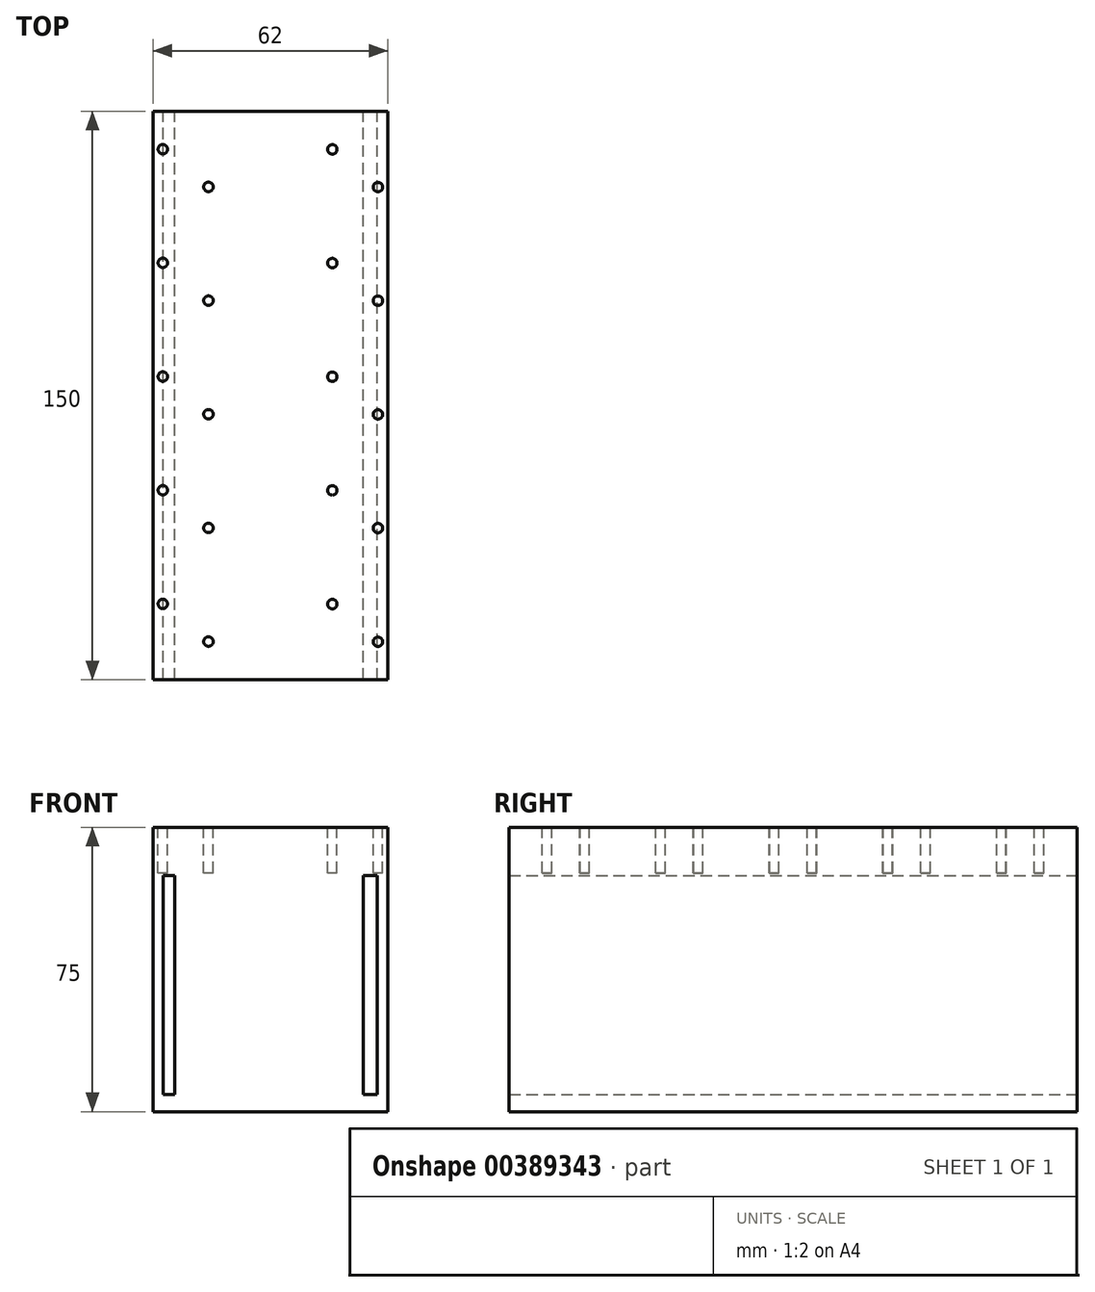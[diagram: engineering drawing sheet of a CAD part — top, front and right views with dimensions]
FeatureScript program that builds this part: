
annotation { "Feature Type Name" : "Feature", "Feature Type Description" : "" }
export const myFeature = defineFeature(function(context is Context, id is Id, definition is map)
    precondition{}
    {
        {
            var Q0;
            Q0=qCreatedBy(makeId("Top.planeOp"),FACE);
            var sketch = newSketch(context, id + "F0", { "sketchPlane" : qUnion([Q0])});
            skLineSegment(sketch, "E0.bottom", {"start": v(31, 75) * mm, "end": v(-31, 75) * mm});
            skLineSegment(sketch, "E0.top", {"start": v(31, -75) * mm, "end": v(-31, -75) * mm});
            skLineSegment(sketch, "E0.left", {"start": v(31, 75) * mm, "end": v(31, -75) * mm});
            skLineSegment(sketch, "E0.right", {"start": v(-31, 75) * mm, "end": v(-31, -75) * mm});
            skPoint(sketch, "E0.middle", {"position": v(0, 0) * mm});
            skCircle(sketch, "E1", {"center": v(-28.4, -55) * mm, "radius": 1.25 * mm});
            skCircle(sketch, "E2", {"center": v(-16.35, -64.95) * mm, "radius": 1.25 * mm});
            skCircle(sketch, "E3", {"center": v(-28.4, -25) * mm, "radius": 1.25 * mm});
            skCircle(sketch, "E4", {"center": v(-16.35, -34.95) * mm, "radius": 1.25 * mm});
            skCircle(sketch, "E5", {"center": v(-28.4, 5) * mm, "radius": 1.25 * mm});
            skCircle(sketch, "E6", {"center": v(-16.35, -4.95) * mm, "radius": 1.25 * mm});
            skCircle(sketch, "E7", {"center": v(-28.4, 35) * mm, "radius": 1.25 * mm});
            skCircle(sketch, "E8", {"center": v(-16.35, 25.05) * mm, "radius": 1.25 * mm});
            skCircle(sketch, "E9", {"center": v(-28.4, 65) * mm, "radius": 1.25 * mm});
            skCircle(sketch, "E10", {"center": v(-16.35, 55.05) * mm, "radius": 1.25 * mm});
            skCircle(sketch, "E11", {"center": v(28.4, 55) * mm, "radius": 1.25 * mm});
            skCircle(sketch, "E12", {"center": v(16.35, 64.95) * mm, "radius": 1.25 * mm});
            skCircle(sketch, "E13", {"center": v(28.4, 25) * mm, "radius": 1.25 * mm});
            skCircle(sketch, "E14", {"center": v(16.35, 34.95) * mm, "radius": 1.25 * mm});
            skCircle(sketch, "E15", {"center": v(28.4, -5) * mm, "radius": 1.25 * mm});
            skCircle(sketch, "E16", {"center": v(16.35, 4.95) * mm, "radius": 1.25 * mm});
            skCircle(sketch, "E17", {"center": v(28.4, -35) * mm, "radius": 1.25 * mm});
            skCircle(sketch, "E18", {"center": v(16.35, -25.05) * mm, "radius": 1.25 * mm});
            skCircle(sketch, "E19", {"center": v(28.4, -65) * mm, "radius": 1.25 * mm});
            skCircle(sketch, "E20", {"center": v(16.35, -55.05) * mm, "radius": 1.25 * mm});
            skSolve(sketch);
        }
        {
            var Q0;
            {var subQ0=sQuery(id+"F0.wireOp",EDGE,"E0.left");var subQ1=sQuery(id+"F0.wireOp",EDGE,"E0.bottom");var subQ2=makeQuery(id+"F0.imprint","INTERSECT",VERTEX,{"derivedFrom":[subQ1,subQ0]});Q0=makeQuery(id+"F0.imprint","IMPRINT",FACE,{"disambiguationData":[TD([[makeQuery(id+"F0.imprint","IMPRINT",EDGE,{"disambiguationData":[TD([[subQ2,-1.0]])],"derivedFrom":subQ0}),-1.0]])]});}
            var Q1;
            Q1=makeQuery(id+"F0.imprint","IMPRINT",FACE,{"disambiguationData":[TD([[makeQuery(id+"F0.imprint","IMPRINT",EDGE,{"derivedFrom":sQuery(id+"F0.wireOp",EDGE,"E11")}),-1.0]])]});
            var Q2;
            {var subQ0=sQuery(id+"F0.wireOp",EDGE,"0Nzpq0zW-OAD0-kYl2-P6jv-PgwHEek2wbxL");var subQ1=sQuery(id+"F0.wireOp",EDGE,"E0.left");var subQ2=makeQuery(id+"F0.imprint","INTERSECT",VERTEX,{"derivedFrom":[subQ1,subQ0]});Q2=makeQuery(id+"F0.imprint","IMPRINT",FACE,{"disambiguationData":[TD([[makeQuery(id+"F0.imprint","IMPRINT",EDGE,{"disambiguationData":[TD([[subQ2,-1.0]])],"derivedFrom":subQ1}),-1.0]])]});}
            var Q3;
            Q3=makeQuery(id+"F0.imprint","IMPRINT",FACE,{"disambiguationData":[TD([[makeQuery(id+"F0.imprint","IMPRINT",EDGE,{"derivedFrom":sQuery(id+"F0.wireOp",EDGE,"E13")}),-1.0]])]});
            var Q4;
            {var subQ0=sQuery(id+"F0.wireOp",EDGE,"HYNGpQ2a-oc8r-ey4b-d9cL-286HAeqs42Th");var subQ1=sQuery(id+"F0.wireOp",EDGE,"E0.left");var subQ2=makeQuery(id+"F0.imprint","INTERSECT",VERTEX,{"derivedFrom":[subQ1,subQ0]});Q4=makeQuery(id+"F0.imprint","IMPRINT",FACE,{"disambiguationData":[TD([[makeQuery(id+"F0.imprint","IMPRINT",EDGE,{"disambiguationData":[TD([[subQ2,-1.0]])],"derivedFrom":subQ1}),-1.0]])]});}
            var Q5;
            Q5=makeQuery(id+"F0.imprint","IMPRINT",FACE,{"disambiguationData":[TD([[makeQuery(id+"F0.imprint","IMPRINT",EDGE,{"derivedFrom":sQuery(id+"F0.wireOp",EDGE,"E15")}),-1.0]])]});
            var Q6;
            {var subQ0=sQuery(id+"F0.wireOp",EDGE,"loNjjLUF-NxmJ-qo9s-MXpg-UicUbD050S6e");var subQ1=sQuery(id+"F0.wireOp",EDGE,"E0.left");var subQ2=makeQuery(id+"F0.imprint","INTERSECT",VERTEX,{"derivedFrom":[subQ1,subQ0]});Q6=makeQuery(id+"F0.imprint","IMPRINT",FACE,{"disambiguationData":[TD([[makeQuery(id+"F0.imprint","IMPRINT",EDGE,{"disambiguationData":[TD([[subQ2,-1.0]])],"derivedFrom":subQ1}),-1.0]])]});}
            var Q7;
            Q7=makeQuery(id+"F0.imprint","IMPRINT",FACE,{"disambiguationData":[TD([[makeQuery(id+"F0.imprint","IMPRINT",EDGE,{"derivedFrom":sQuery(id+"F0.wireOp",EDGE,"E17")}),-1.0]])]});
            var Q8;
            {var subQ0=sQuery(id+"F0.wireOp",EDGE,"7yrL3mt9-zfto-YdMf-zVUi-w2JiUafFn9Ic");var subQ1=sQuery(id+"F0.wireOp",EDGE,"E0.left");var subQ2=makeQuery(id+"F0.imprint","INTERSECT",VERTEX,{"derivedFrom":[subQ1,subQ0]});Q8=makeQuery(id+"F0.imprint","IMPRINT",FACE,{"disambiguationData":[TD([[makeQuery(id+"F0.imprint","IMPRINT",EDGE,{"disambiguationData":[TD([[subQ2,-1.0]])],"derivedFrom":subQ1}),-1.0]])]});}
            var Q9;
            Q9=makeQuery(id+"F0.imprint","IMPRINT",FACE,{"disambiguationData":[TD([[makeQuery(id+"F0.imprint","IMPRINT",EDGE,{"derivedFrom":sQuery(id+"F0.wireOp",EDGE,"E19")}),-1.0]])]});
            var Q10;
            {var subQ0=sQuery(id+"F0.wireOp",EDGE,"E0.left");var subQ1=sQuery(id+"F0.wireOp",EDGE,"E0.top");var subQ2=makeQuery(id+"F0.imprint","INTERSECT",VERTEX,{"derivedFrom":[subQ1,subQ0]});Q10=makeQuery(id+"F0.imprint","IMPRINT",FACE,{"disambiguationData":[TD([[makeQuery(id+"F0.imprint","IMPRINT",EDGE,{"disambiguationData":[TD([[subQ2,1.0]])],"derivedFrom":subQ0}),-1.0]])]});}
            var Q11;
            {var subQ0=sQuery(id+"F0.wireOp",EDGE,"E0.right");var subQ1=sQuery(id+"F0.wireOp",EDGE,"E0.top");var subQ2=makeQuery(id+"F0.imprint","INTERSECT",VERTEX,{"derivedFrom":[subQ1,subQ0]});Q11=makeQuery(id+"F0.imprint","IMPRINT",FACE,{"disambiguationData":[TD([[makeQuery(id+"F0.imprint","IMPRINT",EDGE,{"disambiguationData":[TD([[subQ2,1.0]])],"derivedFrom":subQ0}),1.0]])]});}
            var Q12;
            {var subQ0=sQuery(id+"F0.wireOp",EDGE,"qGLXiPXZ-9OAp-E2Iu-Hi0t-eYRde66machl.right");var subQ1=sQuery(id+"F0.wireOp",EDGE,"nP8XmCDw-qGC3-Xe6r-nWju-59QOWl1pe11c");var subQ2=makeQuery(id+"F0.imprint","INTERSECT",VERTEX,{"derivedFrom":[subQ1,subQ0]});Q12=makeQuery(id+"F0.imprint","IMPRINT",FACE,{"disambiguationData":[TD([[makeQuery(id+"F0.imprint","IMPRINT",EDGE,{"disambiguationData":[TD([[subQ2,-1.0]])],"derivedFrom":subQ1}),1.0]])]});}
            var Q13;
            {var subQ5=sQuery(id+"F0.wireOp",EDGE,"qGLXiPXZ-9OAp-E2Iu-Hi0t-eYRde66machl.top");Q13=makeQuery(id+"F0.imprint","IMPRINT",FACE,{"disambiguationData":[TD([[makeQuery(id+"F0.imprint","IMPRINT",EDGE,{"derivedFrom":subQ5}),1.0]])]});}
            var Q14;
            {var subQ0=sQuery(id+"F0.wireOp",EDGE,"qGLXiPXZ-9OAp-E2Iu-Hi0t-eYRde66machl.right");var subQ1=sQuery(id+"F0.wireOp",EDGE,"7yrL3mt9-zfto-YdMf-zVUi-w2JiUafFn9Ic");var subQ2=makeQuery(id+"F0.imprint","INTERSECT",VERTEX,{"derivedFrom":[subQ1,subQ0]});Q14=makeQuery(id+"F0.imprint","IMPRINT",FACE,{"disambiguationData":[TD([[makeQuery(id+"F0.imprint","IMPRINT",EDGE,{"disambiguationData":[TD([[subQ2,-1.0]])],"derivedFrom":subQ1}),1.0]])]});}
            var Q15;
            {var subQ0=sQuery(id+"F0.wireOp",EDGE,"7yrL3mt9-zfto-YdMf-zVUi-w2JiUafFn9Ic");var subQ1=sQuery(id+"F0.wireOp",EDGE,"E0.right");var subQ2=makeQuery(id+"F0.imprint","INTERSECT",VERTEX,{"derivedFrom":[subQ1,subQ0]});Q15=makeQuery(id+"F0.imprint","IMPRINT",FACE,{"disambiguationData":[TD([[makeQuery(id+"F0.imprint","IMPRINT",EDGE,{"disambiguationData":[TD([[subQ2,-1.0]])],"derivedFrom":subQ1}),1.0]])]});}
            var Q16;
            Q16=makeQuery(id+"F0.imprint","IMPRINT",FACE,{"disambiguationData":[TD([[makeQuery(id+"F0.imprint","IMPRINT",EDGE,{"derivedFrom":sQuery(id+"F0.wireOp",EDGE,"E1")}),-1.0]])]});
            var Q17;
            Q17=makeQuery(id+"F0.imprint","IMPRINT",FACE,{"disambiguationData":[TD([[makeQuery(id+"F0.imprint","IMPRINT",EDGE,{"derivedFrom":sQuery(id+"F0.wireOp",EDGE,"E3")}),-1.0]])]});
            var Q18;
            {var subQ0=sQuery(id+"F0.wireOp",EDGE,"qGLXiPXZ-9OAp-E2Iu-Hi0t-eYRde66machl.right");var subQ1=sQuery(id+"F0.wireOp",EDGE,"dSloDgUL-mvlv-v9cq-rGvp-w3UJGFUMceEQ");var subQ2=makeQuery(id+"F0.imprint","INTERSECT",VERTEX,{"derivedFrom":[subQ1,subQ0]});Q18=makeQuery(id+"F0.imprint","IMPRINT",FACE,{"disambiguationData":[TD([[makeQuery(id+"F0.imprint","IMPRINT",EDGE,{"disambiguationData":[TD([[subQ2,-1.0]])],"derivedFrom":subQ1}),1.0]])]});}
            var Q19;
            {var subQ0=sQuery(id+"F0.wireOp",EDGE,"qGLXiPXZ-9OAp-E2Iu-Hi0t-eYRde66machl.right");var subQ1=sQuery(id+"F0.wireOp",EDGE,"loNjjLUF-NxmJ-qo9s-MXpg-UicUbD050S6e");var subQ2=makeQuery(id+"F0.imprint","INTERSECT",VERTEX,{"derivedFrom":[subQ1,subQ0]});Q19=makeQuery(id+"F0.imprint","IMPRINT",FACE,{"disambiguationData":[TD([[makeQuery(id+"F0.imprint","IMPRINT",EDGE,{"disambiguationData":[TD([[subQ2,-1.0]])],"derivedFrom":subQ1}),1.0]])]});}
            var Q20;
            {var subQ0=sQuery(id+"F0.wireOp",EDGE,"loNjjLUF-NxmJ-qo9s-MXpg-UicUbD050S6e");var subQ1=sQuery(id+"F0.wireOp",EDGE,"E0.right");var subQ2=makeQuery(id+"F0.imprint","INTERSECT",VERTEX,{"derivedFrom":[subQ1,subQ0]});Q20=makeQuery(id+"F0.imprint","IMPRINT",FACE,{"disambiguationData":[TD([[makeQuery(id+"F0.imprint","IMPRINT",EDGE,{"disambiguationData":[TD([[subQ2,-1.0]])],"derivedFrom":subQ1}),1.0]])]});}
            var Q21;
            Q21=makeQuery(id+"F0.imprint","IMPRINT",FACE,{"disambiguationData":[TD([[makeQuery(id+"F0.imprint","IMPRINT",EDGE,{"derivedFrom":sQuery(id+"F0.wireOp",EDGE,"E5")}),-1.0]])]});
            var Q22;
            {var subQ0=sQuery(id+"F0.wireOp",EDGE,"qGLXiPXZ-9OAp-E2Iu-Hi0t-eYRde66machl.right");var subQ1=sQuery(id+"F0.wireOp",EDGE,"gBA85ZTb-Fysj-9ieW-Ogb6-hbMJ70rOvonQ");var subQ2=makeQuery(id+"F0.imprint","INTERSECT",VERTEX,{"derivedFrom":[subQ1,subQ0]});Q22=makeQuery(id+"F0.imprint","IMPRINT",FACE,{"disambiguationData":[TD([[makeQuery(id+"F0.imprint","IMPRINT",EDGE,{"disambiguationData":[TD([[subQ2,-1.0]])],"derivedFrom":subQ1}),1.0]])]});}
            var Q23;
            {var subQ0=sQuery(id+"F0.wireOp",EDGE,"qGLXiPXZ-9OAp-E2Iu-Hi0t-eYRde66machl.right");var subQ1=sQuery(id+"F0.wireOp",EDGE,"HYNGpQ2a-oc8r-ey4b-d9cL-286HAeqs42Th");var subQ2=makeQuery(id+"F0.imprint","INTERSECT",VERTEX,{"derivedFrom":[subQ1,subQ0]});Q23=makeQuery(id+"F0.imprint","IMPRINT",FACE,{"disambiguationData":[TD([[makeQuery(id+"F0.imprint","IMPRINT",EDGE,{"disambiguationData":[TD([[subQ2,-1.0]])],"derivedFrom":subQ1}),1.0]])]});}
            var Q24;
            {var subQ0=sQuery(id+"F0.wireOp",EDGE,"HYNGpQ2a-oc8r-ey4b-d9cL-286HAeqs42Th");var subQ1=sQuery(id+"F0.wireOp",EDGE,"E0.right");var subQ2=makeQuery(id+"F0.imprint","INTERSECT",VERTEX,{"derivedFrom":[subQ1,subQ0]});Q24=makeQuery(id+"F0.imprint","IMPRINT",FACE,{"disambiguationData":[TD([[makeQuery(id+"F0.imprint","IMPRINT",EDGE,{"disambiguationData":[TD([[subQ2,-1.0]])],"derivedFrom":subQ1}),1.0]])]});}
            var Q25;
            Q25=makeQuery(id+"F0.imprint","IMPRINT",FACE,{"disambiguationData":[TD([[makeQuery(id+"F0.imprint","IMPRINT",EDGE,{"derivedFrom":sQuery(id+"F0.wireOp",EDGE,"E7")}),-1.0]])]});
            var Q26;
            {var subQ0=sQuery(id+"F0.wireOp",EDGE,"qGLXiPXZ-9OAp-E2Iu-Hi0t-eYRde66machl.right");var subQ1=sQuery(id+"F0.wireOp",EDGE,"HYNGpQ2a-oc8r-ey4b-d9cL-286HAeqs42Th");var subQ2=makeQuery(id+"F0.imprint","INTERSECT",VERTEX,{"derivedFrom":[subQ1,subQ0]});Q26=makeQuery(id+"F0.imprint","IMPRINT",FACE,{"disambiguationData":[TD([[makeQuery(id+"F0.imprint","IMPRINT",EDGE,{"disambiguationData":[TD([[subQ2,-1.0]])],"derivedFrom":subQ1}),-1.0]])]});}
            var Q27;
            {var subQ0=sQuery(id+"F0.wireOp",EDGE,"qGLXiPXZ-9OAp-E2Iu-Hi0t-eYRde66machl.right");var subQ1=sQuery(id+"F0.wireOp",EDGE,"0Nzpq0zW-OAD0-kYl2-P6jv-PgwHEek2wbxL");var subQ2=makeQuery(id+"F0.imprint","INTERSECT",VERTEX,{"derivedFrom":[subQ1,subQ0]});Q27=makeQuery(id+"F0.imprint","IMPRINT",FACE,{"disambiguationData":[TD([[makeQuery(id+"F0.imprint","IMPRINT",EDGE,{"disambiguationData":[TD([[subQ2,-1.0]])],"derivedFrom":subQ1}),1.0]])]});}
            var Q28;
            {var subQ0=sQuery(id+"F0.wireOp",EDGE,"0Nzpq0zW-OAD0-kYl2-P6jv-PgwHEek2wbxL");var subQ1=sQuery(id+"F0.wireOp",EDGE,"E0.right");var subQ2=makeQuery(id+"F0.imprint","INTERSECT",VERTEX,{"derivedFrom":[subQ1,subQ0]});Q28=makeQuery(id+"F0.imprint","IMPRINT",FACE,{"disambiguationData":[TD([[makeQuery(id+"F0.imprint","IMPRINT",EDGE,{"disambiguationData":[TD([[subQ2,-1.0]])],"derivedFrom":subQ1}),1.0]])]});}
            var Q29;
            Q29=makeQuery(id+"F0.imprint","IMPRINT",FACE,{"disambiguationData":[TD([[makeQuery(id+"F0.imprint","IMPRINT",EDGE,{"derivedFrom":sQuery(id+"F0.wireOp",EDGE,"E9")}),-1.0]])]});
            var Q30;
            {var subQ0=sQuery(id+"F0.wireOp",EDGE,"E0.right");var subQ1=sQuery(id+"F0.wireOp",EDGE,"E0.bottom");var subQ2=makeQuery(id+"F0.imprint","INTERSECT",VERTEX,{"derivedFrom":[subQ1,subQ0]});Q30=makeQuery(id+"F0.imprint","IMPRINT",FACE,{"disambiguationData":[TD([[makeQuery(id+"F0.imprint","IMPRINT",EDGE,{"disambiguationData":[TD([[subQ2,-1.0]])],"derivedFrom":subQ0}),1.0]])]});}
            var Q31;
            {var subQ5=sQuery(id+"F0.wireOp",EDGE,"qGLXiPXZ-9OAp-E2Iu-Hi0t-eYRde66machl.bottom");Q31=makeQuery(id+"F0.imprint","IMPRINT",FACE,{"disambiguationData":[TD([[makeQuery(id+"F0.imprint","IMPRINT",EDGE,{"derivedFrom":subQ5}),-1.0]])]});}
            var Q32;
            {var subQ0=sQuery(id+"F0.wireOp",EDGE,"qGLXiPXZ-9OAp-E2Iu-Hi0t-eYRde66machl.left");var subQ1=sQuery(id+"F0.wireOp",EDGE,"L3z1uPey-24MH-891N-87aN-zqV0T9BSITQc");var subQ2=makeQuery(id+"F0.imprint","INTERSECT",VERTEX,{"derivedFrom":[subQ1,subQ0]});Q32=makeQuery(id+"F0.imprint","IMPRINT",FACE,{"disambiguationData":[TD([[makeQuery(id+"F0.imprint","IMPRINT",EDGE,{"disambiguationData":[TD([[subQ2,-1.0]])],"derivedFrom":subQ1}),-1.0]])]});}
            extrude(context, id + "F1", {"entities" : qUnion([Q0, Q1, Q2, Q3, Q4, Q5, Q6, Q7, Q8, Q9, Q10, Q11, Q12, Q13, Q14, Q15, Q16, Q17, Q18, Q19, Q20, Q21, Q22, Q23, Q24, Q25, Q26, Q27, Q28, Q29, Q30, Q31, Q32]), "oppositeDirection" : true, "depth" : 12 * mm});
        }
        {
            var Q0;
            Q0=makeQuery(id+"F1.opExtrude","CAP_FACE",FACE,{"disambiguationData":[OSD([sQuery(id+"F0.wireOp",EDGE,"E0.bottom"),sQuery(id+"F0.wireOp",EDGE,"E0.top"),sQuery(id+"F0.wireOp",EDGE,"E0.left"),sQuery(id+"F0.wireOp",EDGE,"E0.right"),sQuery(id+"F0.wireOp",EDGE,"qGLXiPXZ-9OAp-E2Iu-Hi0t-eYRde66machl.bottom"),sQuery(id+"F0.wireOp",EDGE,"qGLXiPXZ-9OAp-E2Iu-Hi0t-eYRde66machl.top"),sQuery(id+"F0.wireOp",EDGE,"E1"),sQuery(id+"F0.wireOp",EDGE,"E2"),sQuery(id+"F0.wireOp",EDGE,"E3"),sQuery(id+"F0.wireOp",EDGE,"E4"),sQuery(id+"F0.wireOp",EDGE,"E5"),sQuery(id+"F0.wireOp",EDGE,"E6"),sQuery(id+"F0.wireOp",EDGE,"E7"),sQuery(id+"F0.wireOp",EDGE,"E8"),sQuery(id+"F0.wireOp",EDGE,"E9"),sQuery(id+"F0.wireOp",EDGE,"E10"),sQuery(id+"F0.wireOp",EDGE,"E11"),sQuery(id+"F0.wireOp",EDGE,"E12"),sQuery(id+"F0.wireOp",EDGE,"E13"),sQuery(id+"F0.wireOp",EDGE,"E14"),sQuery(id+"F0.wireOp",EDGE,"E15"),sQuery(id+"F0.wireOp",EDGE,"E16"),sQuery(id+"F0.wireOp",EDGE,"E17"),sQuery(id+"F0.wireOp",EDGE,"E18"),sQuery(id+"F0.wireOp",EDGE,"E19"),sQuery(id+"F0.wireOp",EDGE,"E20")])],"isStart":false});
            var sketch = newSketch(context, id + "F2", { "sketchPlane" : qUnion([Q0])});
            skLineSegment(sketch, "E21.bottom", {"start": v(31, 75) * mm, "end": v(-31, 75) * mm});
            skLineSegment(sketch, "E21.top", {"start": v(31, -75) * mm, "end": v(-31, -75) * mm});
            skLineSegment(sketch, "E21.left", {"start": v(31, 75) * mm, "end": v(31, -75) * mm});
            skLineSegment(sketch, "E21.right", {"start": v(-31, 75) * mm, "end": v(-31, -75) * mm});
            skSolve(sketch);
        }
        {
            var Q0;
            Q0 = qSketchRegion(id + "F2", true);
            extrude(context, id + "F3", {"entities" : qUnion([Q0]), "operationType" : NewBodyOperationType.ADD, "depth" : 63 * mm});
        }
        {
            var Q0;
            Q0=makeQuery(id+"F3.boolean.opBoolean","MERGE",FACE,{"derivedFrom":[makeQuery(id+"F1.opExtrude","SWEPT_FACE",FACE,{"disambiguationData":[OSD([sQuery(id+"F0.wireOp",EDGE,"E0.bottom"),sQuery(id+"F0.wireOp",EDGE,"qGLXiPXZ-9OAp-E2Iu-Hi0t-eYRde66machl.bottom")])]}),makeQuery(id+"F3.opExtrude","SWEPT_FACE",FACE,{"disambiguationData":[OSD([sQuery(id+"F2.wireOp",EDGE,"E21.top")])]})]});
            var sketch = newSketch(context, id + "F4", { "sketchPlane" : qUnion([Q0])});
            skLineSegment(sketch, "E22.bottom", {"start": v(28.27, -12.67) * mm, "end": v(-28.27, -12.67) * mm});
            skLineSegment(sketch, "E22.top", {"start": v(28.27, -70.52) * mm, "end": v(-28.27, -70.52) * mm});
            skLineSegment(sketch, "E22.left", {"start": v(28.27, -12.67) * mm, "end": v(28.27, -70.52) * mm});
            skLineSegment(sketch, "E22.right", {"start": v(-28.27, -12.67) * mm, "end": v(-28.27, -70.52) * mm});
            skPoint(sketch, "E22.middle", {"position": v(0, -41.6) * mm});
            skLineSegment(sketch, "E23.bottom", {"start": v(3.23, -12.67) * mm, "end": v(-3.23, -12.67) * mm});
            skLineSegment(sketch, "E23.top", {"start": v(3.23, -70.52) * mm, "end": v(-3.23, -70.52) * mm});
            skLineSegment(sketch, "E23.left", {"start": v(3.23, -12.67) * mm, "end": v(3.23, -70.52) * mm});
            skLineSegment(sketch, "E23.right", {"start": v(-3.23, -12.67) * mm, "end": v(-3.23, -70.52) * mm});
            skLineSegment(sketch, "E24.bottom", {"start": v(-22.33, -70.52) * mm, "end": v(-15.95, -70.52) * mm});
            skLineSegment(sketch, "E24.top", {"start": v(-22.33, -12.67) * mm, "end": v(-15.95, -12.67) * mm});
            skLineSegment(sketch, "E24.left", {"start": v(-22.33, -70.52) * mm, "end": v(-22.33, -12.67) * mm});
            skLineSegment(sketch, "E24.right", {"start": v(-15.95, -70.52) * mm, "end": v(-15.95, -12.67) * mm});
            skLineSegment(sketch, "E25.bottom", {"start": v(-13.36, -12.67) * mm, "end": v(-5.91, -12.67) * mm});
            skLineSegment(sketch, "E25.top", {"start": v(-13.36, -70.52) * mm, "end": v(-5.91, -70.52) * mm});
            skLineSegment(sketch, "E25.left", {"start": v(-13.36, -12.67) * mm, "end": v(-13.36, -70.52) * mm});
            skLineSegment(sketch, "E25.right", {"start": v(-5.91, -12.67) * mm, "end": v(-5.91, -70.52) * mm});
            skLineSegment(sketch, "E26.bottom", {"start": v(5.64, -12.67) * mm, "end": v(13.09, -12.67) * mm});
            skLineSegment(sketch, "E26.top", {"start": v(5.64, -70.52) * mm, "end": v(13.09, -70.52) * mm});
            skLineSegment(sketch, "E26.left", {"start": v(5.64, -12.67) * mm, "end": v(5.64, -70.52) * mm});
            skLineSegment(sketch, "E26.right", {"start": v(13.09, -12.67) * mm, "end": v(13.09, -70.52) * mm});
            skLineSegment(sketch, "E27.bottom", {"start": v(15.32, -12.67) * mm, "end": v(22.93, -12.67) * mm});
            skLineSegment(sketch, "E27.top", {"start": v(15.32, -70.52) * mm, "end": v(22.93, -70.52) * mm});
            skLineSegment(sketch, "E27.left", {"start": v(15.32, -12.67) * mm, "end": v(15.32, -70.52) * mm});
            skLineSegment(sketch, "E27.right", {"start": v(22.93, -12.67) * mm, "end": v(22.93, -70.52) * mm});
            skLineSegment(sketch, "E28", {"start": v(-24.47, -12.67) * mm, "end": v(-24.47, -70.52) * mm});
            skLineSegment(sketch, "E29", {"start": v(25.3, -12.67) * mm, "end": v(25.3, -70.52) * mm});
            skSolve(sketch);
        }
        {
            var Q0;
            {var subQ0=sQuery(id+"F4.wireOp",EDGE,"E22.right");Q0=makeQuery(id+"F4.imprint","IMPRINT",FACE,{"disambiguationData":[TD([[makeQuery(id+"F4.imprint","IMPRINT",EDGE,{"derivedFrom":subQ0}),1.0]])]});}
            var Q1;
            Q1=makeQuery(id+"F4.imprint","IMPRINT",FACE,{"disambiguationData":[TD([[makeQuery(id+"F4.imprint","IMPRINT",EDGE,{"derivedFrom":sQuery(id+"F4.wireOp",EDGE,"E24.bottom")}),1.0]])]});
            var Q2;
            Q2=makeQuery(id+"F4.imprint","IMPRINT",FACE,{"disambiguationData":[TD([[makeQuery(id+"F4.imprint","IMPRINT",EDGE,{"derivedFrom":sQuery(id+"F4.wireOp",EDGE,"E25.bottom")}),-1.0]])]});
            var Q3;
            Q3=makeQuery(id+"F4.imprint","IMPRINT",FACE,{"disambiguationData":[TD([[makeQuery(id+"F4.imprint","IMPRINT",EDGE,{"derivedFrom":sQuery(id+"F4.wireOp",EDGE,"E23.bottom")}),1.0]])]});
            var Q4;
            Q4=makeQuery(id+"F4.imprint","IMPRINT",FACE,{"disambiguationData":[TD([[makeQuery(id+"F4.imprint","IMPRINT",EDGE,{"derivedFrom":sQuery(id+"F4.wireOp",EDGE,"E26.bottom")}),-1.0]])]});
            var Q5;
            Q5=makeQuery(id+"F4.imprint","IMPRINT",FACE,{"disambiguationData":[TD([[makeQuery(id+"F4.imprint","IMPRINT",EDGE,{"derivedFrom":sQuery(id+"F4.wireOp",EDGE,"E27.bottom")}),-1.0]])]});
            var Q6;
            {var subQ0=sQuery(id+"F4.wireOp",EDGE,"E22.left");Q6=makeQuery(id+"F4.imprint","IMPRINT",FACE,{"disambiguationData":[TD([[makeQuery(id+"F4.imprint","IMPRINT",EDGE,{"derivedFrom":subQ0}),-1.0]])]});}
            extrude(context, id + "F5", {"entities" : qUnion([Q0, Q1, Q2, Q3, Q4, Q5, Q6]), "operationType" : NewBodyOperationType.REMOVE, "oppositeDirection" : true, "depth" : 150 * mm});
        }
    });
